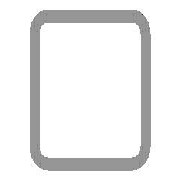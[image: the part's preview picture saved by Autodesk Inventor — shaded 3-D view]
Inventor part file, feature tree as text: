
AUTODESK INVENTOR PART (.ipt)
format: ipt  version: 2022 (Build 260153000, 153)  size: 134,656 bytes
history: native  units: mm (DEFAULTED — no unit token found)
features: other x4, sketch x3, extrude x1, plane x1
ambient origin geometry x8: Origin, YZ Plane, XZ Plane, XY Plane, X Axis, Y Axis, Z Axis, Center Point
bodies: Solid1 (feature_tree)
feature tree (9):
  parser-record x1  (decoder bookkeeping rows leaked as tree rows — omitted from the tree; the rows remain in map.json)
  other  "Driven Length"
  other  "Plano inicial"
  other  "Plano final"
  extrude  "Cuerpo"  TaperAngle=0.0deg  [1 undecoded]
  sketch  "Boceto"  dims[d10=40.0mm d11=40.0mm d12=5.0mm d13=-0.0mm d14=575.0mm d15=20.0mm d16=20.0mm d17=90.0deg d18=575.0mm]
  sketch  "Sketch3"  dims[d3=575.0mm d4=0.0mm]
  plane  "Work Plane3"
  sketch  "Sketch4"  dims[d7=7.5mm]
note: 1 required parameter value undecoded (feature->parameter linkage not recoverable at this tier; creation-order binding heuristic only, values carry confidence <= 0.55)
